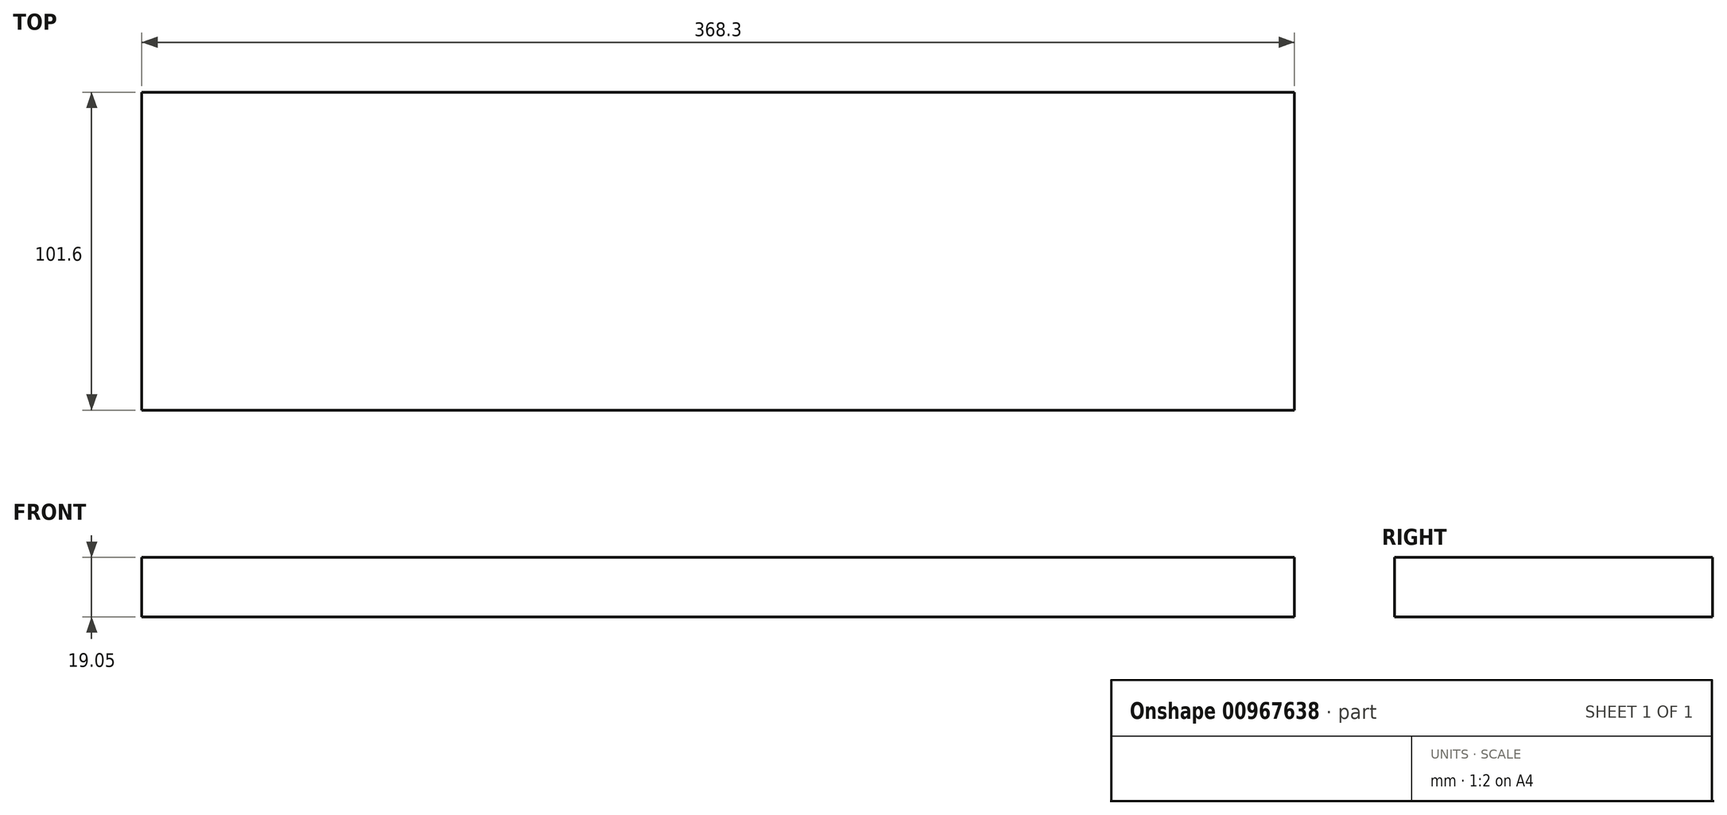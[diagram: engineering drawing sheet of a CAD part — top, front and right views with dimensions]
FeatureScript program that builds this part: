
annotation { "Feature Type Name" : "Feature", "Feature Type Description" : "" }
export const myFeature = defineFeature(function(context is Context, id is Id, definition is map)
    precondition{}
    {
        {
            var Q0;
            Q0=qCreatedBy(makeId("Top.planeOp"),FACE);
            var sketch = newSketch(context, id + "F0", { "sketchPlane" : qUnion([Q0])});
            skLineSegment(sketch, "E0.bottom", {"start": v(0, 0) * mm, "end": v(368.3, 0) * mm});
            skLineSegment(sketch, "E0.top", {"start": v(0, -101.6) * mm, "end": v(368.3, -101.6) * mm});
            skLineSegment(sketch, "E0.left", {"start": v(0, 0) * mm, "end": v(0, -101.6) * mm});
            skLineSegment(sketch, "E0.right", {"start": v(368.3, 0) * mm, "end": v(368.3, -101.6) * mm});
            skSolve(sketch);
        }
        {
            var Q0;
            Q0 = qSketchRegion(id + "F0", true);
            extrude(context, id + "F1", {"entities" : qUnion([Q0]), "depth" : 19.05 * mm, "offsetDistance" : 25.4 * mm});
        }
    });
